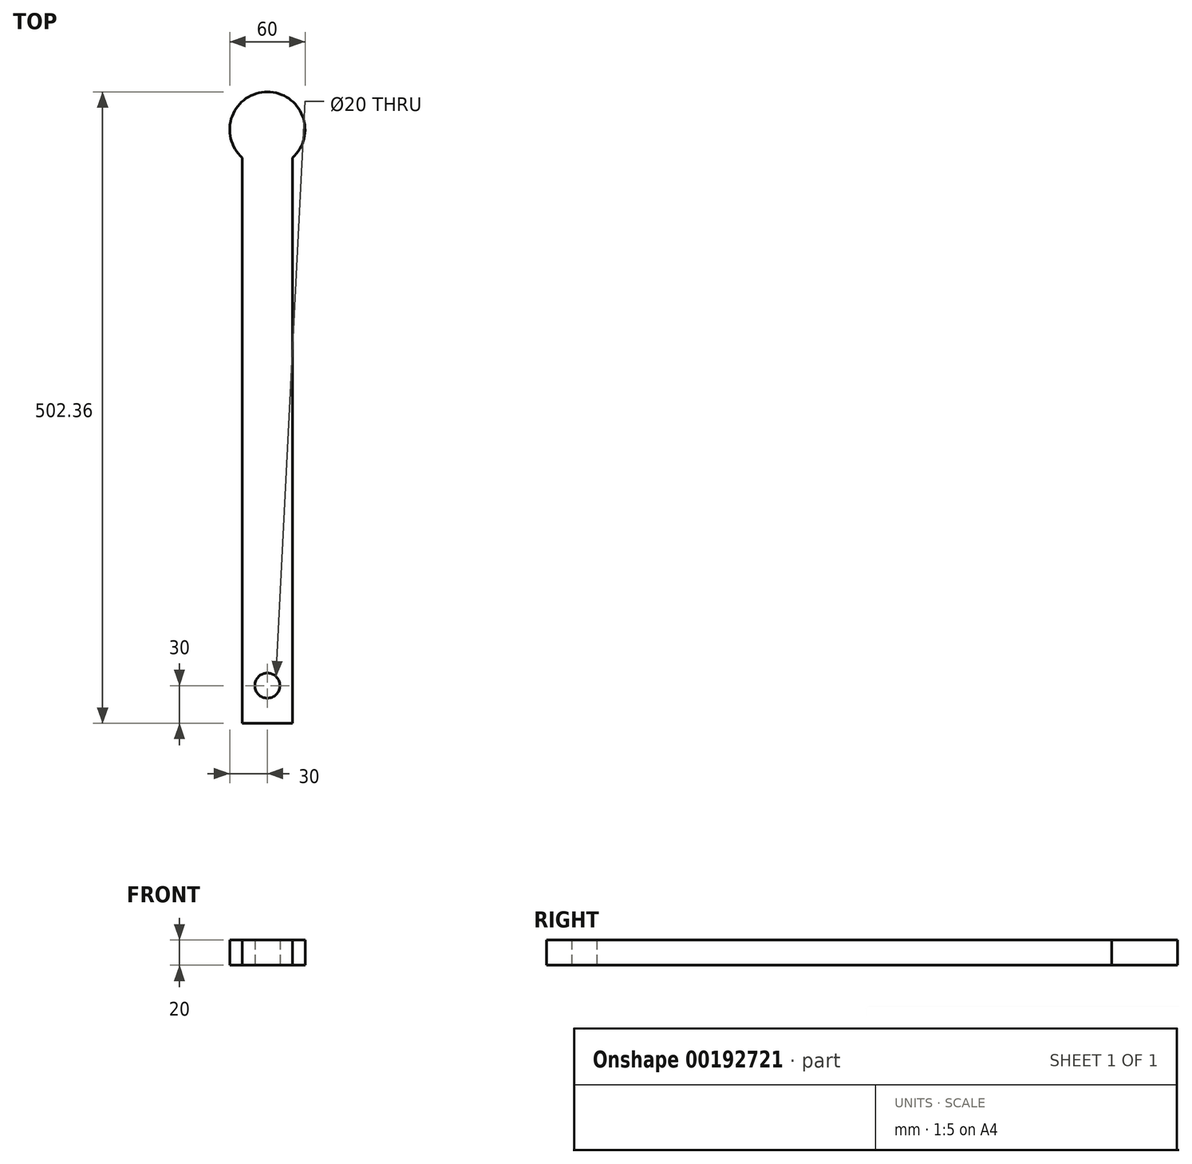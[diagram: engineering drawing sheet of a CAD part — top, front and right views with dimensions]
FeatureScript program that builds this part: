
annotation { "Feature Type Name" : "Feature", "Feature Type Description" : "" }
export const myFeature = defineFeature(function(context is Context, id is Id, definition is map)
    precondition{}
    {
        {
            var Q0;
            Q0=qCreatedBy(makeId("Top.planeOp"),FACE);
            var sketch = newSketch(context, id + "F0", { "sketchPlane" : qUnion([Q0])});
            skLineSegment(sketch, "E0", {"start": v(0, 0) * mm, "end": v(20, 0) * mm});
            skLineSegment(sketch, "E1", {"start": v(20, 0) * mm, "end": v(20, 450) * mm});
            skLineSegment(sketch, "E2", {"start": v(0, 0) * mm, "end": v(0, 38.4) * mm, "construction": true});
            skLineSegment(sketch, "E3.MirrorCS", {"start": v(0, 0) * mm, "end": v(-20, 0) * mm});
            skLineSegment(sketch, "E4.MirrorCS", {"start": v(-20, 0) * mm, "end": v(-20, 450) * mm});
            skArc(sketch, "E5", {"start": v(20, 450) * mm, "mid": v(0, 502.36) * mm, "end": v(-20, 450) * mm});
            skSolve(sketch);
        }
        {
            var Q0;
            Q0 = qSketchRegion(id + "F0", true);
            extrude(context, id + "F1", {"entities" : qUnion([Q0]), "depth" : 20 * mm});
        }
        {
            var Q0;
            Q0=makeQuery(id+"F1.opExtrude","CAP_FACE",FACE,{"disambiguationData":[OSD([sQuery(id+"F0.wireOp",EDGE,"E0"),sQuery(id+"F0.wireOp",EDGE,"E1"),sQuery(id+"F0.wireOp",EDGE,"E3.MirrorCS"),sQuery(id+"F0.wireOp",EDGE,"E4.MirrorCS"),sQuery(id+"F0.wireOp",EDGE,"E5")])],"isStart":true});
            var sketch = newSketch(context, id + "F2", { "sketchPlane" : qUnion([Q0])});
            skLineSegment(sketch, "E6", {"start": v(0, 0) * mm, "end": v(0, -30) * mm, "construction": true});
            skCircle(sketch, "E7", {"center": v(0, -30) * mm, "radius": 10 * mm});
            skSolve(sketch);
        }
        {
            var Q0;
            Q0 = qSketchRegion(id + "F2", true);
            extrude(context, id + "F3", {"entities" : qUnion([Q0]), "operationType" : NewBodyOperationType.REMOVE, "endBound" : BoundingType.THROUGH_ALL, "oppositeDirection" : true, "depth" : 25 * mm});
        }
    });
